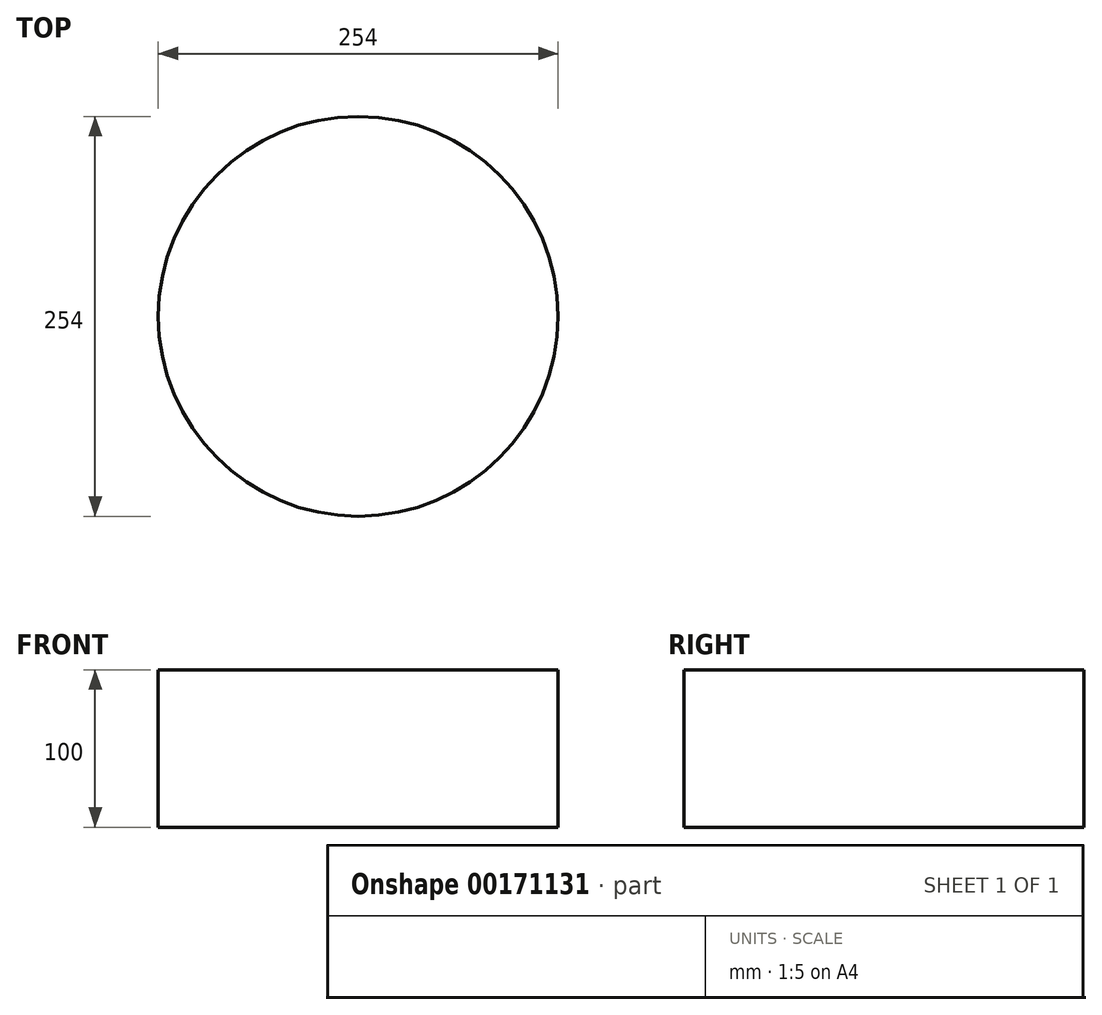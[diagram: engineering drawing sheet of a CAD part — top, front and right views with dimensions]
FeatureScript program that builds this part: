
annotation { "Feature Type Name" : "Feature", "Feature Type Description" : "" }
export const myFeature = defineFeature(function(context is Context, id is Id, definition is map)
    precondition{}
    {
        {
            var Q0;
            Q0=qCreatedBy(makeId("Top.planeOp"),FACE);
            var sketch = newSketch(context, id + "F0", { "sketchPlane" : qUnion([Q0])});
            skCircle(sketch, "E0", {"center": v(0, 0) * mm, "radius": 127 * mm});
            skSolve(sketch);
        }
        {
            var Q0;
            Q0 = qSketchRegion(id + "F0", true);
            extrude(context, id + "F1", {"entities" : qUnion([Q0]), "depth" : 100 * mm});
        }
    });
